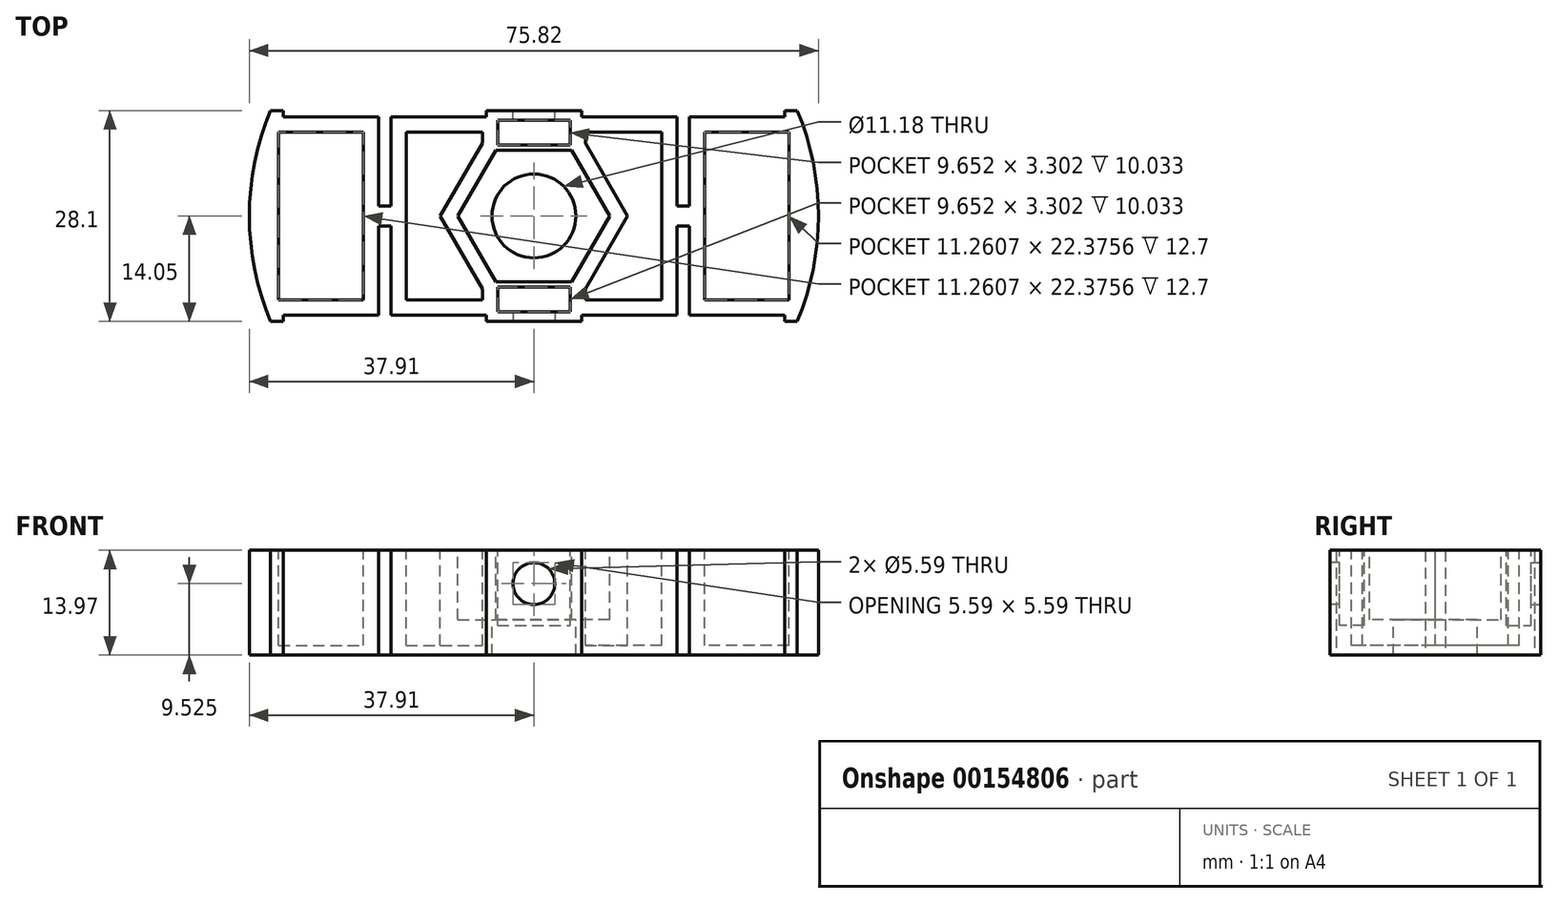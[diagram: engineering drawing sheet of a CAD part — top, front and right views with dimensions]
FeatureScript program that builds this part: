
annotation { "Feature Type Name" : "Feature", "Feature Type Description" : "" }
export const myFeature = defineFeature(function(context is Context, id is Id, definition is map)
    precondition{}
    {
        {
            var Q0;
            Q0=qCreatedBy(makeId("Top.planeOp"),FACE);
            var sketch = newSketch(context, id + "F0", { "sketchPlane" : qUnion([Q0])});
            skLineSegment(sketch, "E0", {"start": v(-37.9, 0) * mm, "end": v(0, 0) * mm, "construction": true});
            skLineSegment(sketch, "E1", {"start": v(-35.07, 14.05) * mm, "end": v(-33.4, 14.05) * mm});
            skArc(sketch, "E2.trimOffspring", {"start": v(-35.07, 14.05) * mm, "mid": v(-37.2, 7.16) * mm, "end": v(-37.9, 0) * mm});
            skLineSegment(sketch, "E3", {"start": v(-20.7, 13.22) * mm, "end": v(-20.7, 1.35) * mm});
            skLineSegment(sketch, "E4", {"start": v(-20.7, 1.35) * mm, "end": v(-19.05, 1.35) * mm});
            skLineSegment(sketch, "E5", {"start": v(-19.05, 1.35) * mm, "end": v(-19.05, 13.22) * mm});
            skLineSegment(sketch, "E6", {"start": v(-19.05, 13.22) * mm, "end": v(-6.35, 13.22) * mm});
            skLineSegment(sketch, "E7", {"start": v(-6.35, 13.22) * mm, "end": v(-6.35, 14.05) * mm});
            skLineSegment(sketch, "E8", {"start": v(-20.7, 13.22) * mm, "end": v(-33.4, 13.22) * mm});
            skLineSegment(sketch, "E9", {"start": v(-33.4, 13.22) * mm, "end": v(-33.4, 14.05) * mm});
            skLineSegment(sketch, "E10.trimOffspring", {"start": v(-6.35, 14.05) * mm, "end": v(0, 14.05) * mm});
            skLineSegment(sketch, "E11", {"start": v(0, 14.05) * mm, "end": v(0, 0) * mm, "construction": true});
            skLineSegment(sketch, "E12.MirrorCS", {"start": v(0, -14.05) * mm, "end": v(0, 0) * mm, "construction": true});
            skPoint(sketch, "E13.MirrorCS.end.orphan", {"position": v(-37.9, 0) * mm});
            skLineSegment(sketch, "E14", {"start": v(-37.9, 0) * mm, "end": v(0, 0) * mm});
            skLineSegment(sketch, "E15", {"start": v(0, 14.05) * mm, "end": v(0, 0) * mm});
            skSolve(sketch);
        }
        {
            var Q0;
            Q0 = qSketchRegion(id + "F0", true);
            extrude(context, id + "F1", {"entities" : qUnion([Q0]), "depth" : 9.52 * mm});
        }
        {
            var Q0;
            Q0=makeQuery(id+"F1.opExtrude","CAP_FACE",FACE,{"disambiguationData":[OSD([sQuery(id+"F0.wireOp",EDGE,"E1"),sQuery(id+"F0.wireOp",EDGE,"E2.trimOffspring"),sQuery(id+"F0.wireOp",EDGE,"E3"),sQuery(id+"F0.wireOp",EDGE,"E4"),sQuery(id+"F0.wireOp",EDGE,"E5"),sQuery(id+"F0.wireOp",EDGE,"E6"),sQuery(id+"F0.wireOp",EDGE,"E7"),sQuery(id+"F0.wireOp",EDGE,"E8"),sQuery(id+"F0.wireOp",EDGE,"E9"),sQuery(id+"F0.wireOp",EDGE,"E10.trimOffspring"),sQuery(id+"F0.wireOp",EDGE,"17128e08-2a4f-4ac8-b99a-ad05750c33720.MirrorCS"),sQuery(id+"F0.wireOp",EDGE,"17128e08-2a4f-4ac8-b99a-ad05750c33721.MirrorCS"),sQuery(id+"F0.wireOp",EDGE,"17128e08-2a4f-4ac8-b99a-ad05750c33722.MirrorCS"),sQuery(id+"F0.wireOp",EDGE,"17128e08-2a4f-4ac8-b99a-ad05750c33723.MirrorCS"),sQuery(id+"F0.wireOp",EDGE,"17128e08-2a4f-4ac8-b99a-ad05750c33724.MirrorCS"),sQuery(id+"F0.wireOp",EDGE,"17128e08-2a4f-4ac8-b99a-ad05750c33725.MirrorCS"),sQuery(id+"F0.wireOp",EDGE,"17128e08-2a4f-4ac8-b99a-ad05750c33726.MirrorCS"),sQuery(id+"F0.wireOp",EDGE,"17128e08-2a4f-4ac8-b99a-ad05750c33727.MirrorCS"),sQuery(id+"F0.wireOp",EDGE,"17128e08-2a4f-4ac8-b99a-ad05750c33728.MirrorCS"),sQuery(id+"F0.wireOp",EDGE,"17128e08-2a4f-4ac8-b99a-ad05750c33729.MirrorCS"),sQuery(id+"F0.wireOp",EDGE,"2adf77e0-dea9-4455-b5b0-009e9eeb048a0.MirrorCS"),sQuery(id+"F0.wireOp",EDGE,"2adf77e0-dea9-4455-b5b0-009e9eeb048a1.MirrorCS"),sQuery(id+"F0.wireOp",EDGE,"2adf77e0-dea9-4455-b5b0-009e9eeb048a2.MirrorCS"),sQuery(id+"F0.wireOp",EDGE,"2adf77e0-dea9-4455-b5b0-009e9eeb048a3.MirrorCS"),sQuery(id+"F0.wireOp",EDGE,"2adf77e0-dea9-4455-b5b0-009e9eeb048a4.MirrorCS"),sQuery(id+"F0.wireOp",EDGE,"2adf77e0-dea9-4455-b5b0-009e9eeb048a5.MirrorCS"),sQuery(id+"F0.wireOp",EDGE,"2adf77e0-dea9-4455-b5b0-009e9eeb048a6.MirrorCS"),sQuery(id+"F0.wireOp",EDGE,"2adf77e0-dea9-4455-b5b0-009e9eeb048a7.MirrorCS"),sQuery(id+"F0.wireOp",EDGE,"2adf77e0-dea9-4455-b5b0-009e9eeb048a8.MirrorCS"),sQuery(id+"F0.wireOp",EDGE,"2adf77e0-dea9-4455-b5b0-009e9eeb048a9.MirrorCS"),sQuery(id+"F0.wireOp",EDGE,"2adf77e0-dea9-4455-b5b0-009e9eeb048a10.MirrorCS"),sQuery(id+"F0.wireOp",EDGE,"2adf77e0-dea9-4455-b5b0-009e9eeb048a11.MirrorCS"),sQuery(id+"F0.wireOp",EDGE,"2adf77e0-dea9-4455-b5b0-009e9eeb048a12.MirrorCS"),sQuery(id+"F0.wireOp",EDGE,"2adf77e0-dea9-4455-b5b0-009e9eeb048a13.MirrorCS"),sQuery(id+"F0.wireOp",EDGE,"2adf77e0-dea9-4455-b5b0-009e9eeb048a15.MirrorCS"),sQuery(id+"F0.wireOp",EDGE,"2adf77e0-dea9-4455-b5b0-009e9eeb048a16.MirrorCS"),sQuery(id+"F0.wireOp",EDGE,"2adf77e0-dea9-4455-b5b0-009e9eeb048a18.MirrorCS"),sQuery(id+"F0.wireOp",EDGE,"2adf77e0-dea9-4455-b5b0-009e9eeb048a19.MirrorCS"),sQuery(id+"F0.wireOp",EDGE,"2adf77e0-dea9-4455-b5b0-009e9eeb048a20.MirrorCS"),sQuery(id+"F0.wireOp",EDGE,"E13.MirrorCS")])],"isStart":false});
            var sketch = newSketch(context, id + "F2", { "sketchPlane" : qUnion([Q0])});
            skCircle(sketch, "E16.cCircle", {"center": v(0, 0) * mm, "radius": 8.9 * mm, "construction": true});
            skLineSegment(sketch, "E16.0", {"start": v(10.27, 0) * mm, "end": v(5.13, -8.9) * mm});
            skLineSegment(sketch, "E16.1", {"start": v(5.13, -8.9) * mm, "end": v(-5.13, -8.89) * mm});
            skLineSegment(sketch, "E16.2", {"start": v(-5.13, -8.9) * mm, "end": v(-10.27, 0) * mm});
            skLineSegment(sketch, "E16.3", {"start": v(-10.27, 0) * mm, "end": v(-5.13, 8.9) * mm});
            skLineSegment(sketch, "E16.4", {"start": v(-5.13, 8.9) * mm, "end": v(5.13, 8.89) * mm});
            skLineSegment(sketch, "E16.5", {"start": v(5.13, 8.9) * mm, "end": v(10.27, 0) * mm});
            skPoint(sketch, "E16.0.midPoint", {"position": v(7.7, -4.45) * mm});
            skSolve(sketch);
        }
        {
            var Q0;
            Q0=makeQuery(id+"F2.imprint","IMPRINT",FACE,{"disambiguationData":[TD([[makeQuery(id+"F2.imprint","IMPRINT",EDGE,{"derivedFrom":sQuery(id+"F2.wireOp",EDGE,"E16.0")}),-1.0]])]});
            extrude(context, id + "F3", {"entities" : qUnion([Q0]), "operationType" : NewBodyOperationType.REMOVE, "oppositeDirection" : true, "depth" : 6.35 * mm});
        }
        {
            var Q0;
            Q0=makeQuery(id+"F1.opExtrude","CAP_FACE",FACE,{"disambiguationData":[OSD([sQuery(id+"F0.wireOp",EDGE,"E1"),sQuery(id+"F0.wireOp",EDGE,"E2.trimOffspring"),sQuery(id+"F0.wireOp",EDGE,"E3"),sQuery(id+"F0.wireOp",EDGE,"E4"),sQuery(id+"F0.wireOp",EDGE,"E5"),sQuery(id+"F0.wireOp",EDGE,"E6"),sQuery(id+"F0.wireOp",EDGE,"E7"),sQuery(id+"F0.wireOp",EDGE,"E8"),sQuery(id+"F0.wireOp",EDGE,"E9"),sQuery(id+"F0.wireOp",EDGE,"E10.trimOffspring"),sQuery(id+"F0.wireOp",EDGE,"17128e08-2a4f-4ac8-b99a-ad05750c33720.MirrorCS"),sQuery(id+"F0.wireOp",EDGE,"17128e08-2a4f-4ac8-b99a-ad05750c33721.MirrorCS"),sQuery(id+"F0.wireOp",EDGE,"17128e08-2a4f-4ac8-b99a-ad05750c33722.MirrorCS"),sQuery(id+"F0.wireOp",EDGE,"17128e08-2a4f-4ac8-b99a-ad05750c33723.MirrorCS"),sQuery(id+"F0.wireOp",EDGE,"17128e08-2a4f-4ac8-b99a-ad05750c33724.MirrorCS"),sQuery(id+"F0.wireOp",EDGE,"17128e08-2a4f-4ac8-b99a-ad05750c33725.MirrorCS"),sQuery(id+"F0.wireOp",EDGE,"17128e08-2a4f-4ac8-b99a-ad05750c33726.MirrorCS"),sQuery(id+"F0.wireOp",EDGE,"17128e08-2a4f-4ac8-b99a-ad05750c33727.MirrorCS"),sQuery(id+"F0.wireOp",EDGE,"17128e08-2a4f-4ac8-b99a-ad05750c33728.MirrorCS"),sQuery(id+"F0.wireOp",EDGE,"17128e08-2a4f-4ac8-b99a-ad05750c33729.MirrorCS"),sQuery(id+"F0.wireOp",EDGE,"2adf77e0-dea9-4455-b5b0-009e9eeb048a0.MirrorCS"),sQuery(id+"F0.wireOp",EDGE,"2adf77e0-dea9-4455-b5b0-009e9eeb048a1.MirrorCS"),sQuery(id+"F0.wireOp",EDGE,"2adf77e0-dea9-4455-b5b0-009e9eeb048a2.MirrorCS"),sQuery(id+"F0.wireOp",EDGE,"2adf77e0-dea9-4455-b5b0-009e9eeb048a3.MirrorCS"),sQuery(id+"F0.wireOp",EDGE,"2adf77e0-dea9-4455-b5b0-009e9eeb048a4.MirrorCS"),sQuery(id+"F0.wireOp",EDGE,"2adf77e0-dea9-4455-b5b0-009e9eeb048a5.MirrorCS"),sQuery(id+"F0.wireOp",EDGE,"2adf77e0-dea9-4455-b5b0-009e9eeb048a6.MirrorCS"),sQuery(id+"F0.wireOp",EDGE,"2adf77e0-dea9-4455-b5b0-009e9eeb048a7.MirrorCS"),sQuery(id+"F0.wireOp",EDGE,"2adf77e0-dea9-4455-b5b0-009e9eeb048a8.MirrorCS"),sQuery(id+"F0.wireOp",EDGE,"2adf77e0-dea9-4455-b5b0-009e9eeb048a9.MirrorCS"),sQuery(id+"F0.wireOp",EDGE,"2adf77e0-dea9-4455-b5b0-009e9eeb048a10.MirrorCS"),sQuery(id+"F0.wireOp",EDGE,"2adf77e0-dea9-4455-b5b0-009e9eeb048a11.MirrorCS"),sQuery(id+"F0.wireOp",EDGE,"2adf77e0-dea9-4455-b5b0-009e9eeb048a12.MirrorCS"),sQuery(id+"F0.wireOp",EDGE,"2adf77e0-dea9-4455-b5b0-009e9eeb048a13.MirrorCS"),sQuery(id+"F0.wireOp",EDGE,"2adf77e0-dea9-4455-b5b0-009e9eeb048a15.MirrorCS"),sQuery(id+"F0.wireOp",EDGE,"2adf77e0-dea9-4455-b5b0-009e9eeb048a16.MirrorCS"),sQuery(id+"F0.wireOp",EDGE,"2adf77e0-dea9-4455-b5b0-009e9eeb048a18.MirrorCS"),sQuery(id+"F0.wireOp",EDGE,"2adf77e0-dea9-4455-b5b0-009e9eeb048a19.MirrorCS"),sQuery(id+"F0.wireOp",EDGE,"2adf77e0-dea9-4455-b5b0-009e9eeb048a20.MirrorCS"),sQuery(id+"F0.wireOp",EDGE,"E13.MirrorCS")])],"isStart":false});
            var sketch = newSketch(context, id + "F4", { "sketchPlane" : qUnion([Q0])});
            skLineSegment(sketch, "E17.bottom", {"start": v(-4.83, -9.47) * mm, "end": v(4.83, -9.47) * mm});
            skLineSegment(sketch, "E17.top", {"start": v(-4.83, -12.78) * mm, "end": v(4.83, -12.78) * mm});
            skLineSegment(sketch, "E17.left", {"start": v(-4.83, -9.47) * mm, "end": v(-4.83, -12.78) * mm});
            skLineSegment(sketch, "E17.right", {"start": v(4.83, -9.47) * mm, "end": v(4.83, -12.78) * mm});
            skLineSegment(sketch, "E18", {"start": v(-12.78, 0) * mm, "end": v(12.46, 0) * mm, "construction": true});
            skLineSegment(sketch, "E19.MirrorCS", {"start": v(-4.83, 9.47) * mm, "end": v(4.83, 9.47) * mm});
            skLineSegment(sketch, "E20.MirrorCS", {"start": v(-4.83, 12.78) * mm, "end": v(4.83, 12.78) * mm});
            skLineSegment(sketch, "E21.MirrorCS", {"start": v(-4.83, 9.47) * mm, "end": v(-4.83, 12.78) * mm});
            skLineSegment(sketch, "E22.MirrorCS", {"start": v(4.83, 9.47) * mm, "end": v(4.83, 12.78) * mm});
            skSolve(sketch);
        }
        {
            var Q0;
            Q0 = qSketchRegion(id + "F4", true);
            extrude(context, id + "F5", {"entities" : qUnion([Q0]), "operationType" : NewBodyOperationType.REMOVE, "oppositeDirection" : true, "depth" : 5.6 * mm});
        }
        {
            var Q0;
            Q0=makeQuery(id+"F1.opExtrude","CAP_FACE",FACE,{"disambiguationData":[OSD([sQuery(id+"F0.wireOp",EDGE,"E1"),sQuery(id+"F0.wireOp",EDGE,"E2.trimOffspring"),sQuery(id+"F0.wireOp",EDGE,"E3"),sQuery(id+"F0.wireOp",EDGE,"E4"),sQuery(id+"F0.wireOp",EDGE,"E5"),sQuery(id+"F0.wireOp",EDGE,"E6"),sQuery(id+"F0.wireOp",EDGE,"E7"),sQuery(id+"F0.wireOp",EDGE,"E8"),sQuery(id+"F0.wireOp",EDGE,"E9"),sQuery(id+"F0.wireOp",EDGE,"E10.trimOffspring"),sQuery(id+"F0.wireOp",EDGE,"E14"),sQuery(id+"F0.wireOp",EDGE,"E15")])],"isStart":false});
            var sketch = newSketch(context, id + "F6", { "sketchPlane" : qUnion([Q0])});
            skCircle(sketch, "E23.cCircle", {"center": v(0, 0) * mm, "radius": 8.76 * mm, "construction": true});
            skLineSegment(sketch, "E23.0", {"start": v(5.06, -8.76) * mm, "end": v(-5.06, -8.76) * mm});
            skLineSegment(sketch, "E23.1", {"start": v(-5.06, -8.76) * mm, "end": v(-10.12, 0) * mm});
            skLineSegment(sketch, "E23.2", {"start": v(-10.12, 0) * mm, "end": v(-5.06, 8.76) * mm});
            skLineSegment(sketch, "E23.3", {"start": v(-5.06, 8.76) * mm, "end": v(5.06, 8.76) * mm});
            skLineSegment(sketch, "E23.4", {"start": v(5.06, 8.76) * mm, "end": v(10.12, 0) * mm});
            skLineSegment(sketch, "E23.5", {"start": v(10.12, 0) * mm, "end": v(5.06, -8.76) * mm});
            skPoint(sketch, "E23.0.midPoint", {"position": v(0, -8.76) * mm});
            skSolve(sketch);
        }
        {
            var Q0;
            Q0 = qSketchRegion(id + "F6", true);
            extrude(context, id + "F7", {"entities" : qUnion([Q0]), "operationType" : NewBodyOperationType.REMOVE, "oppositeDirection" : true, "depth" : 4.83 * mm});
        }
        {
            var Q0;
            Q0=makeQuery(id+"F7.boolean.opBoolean","COPY",FACE,{"derivedFrom":makeQuery(id+"F7.opExtrude","CAP_FACE",FACE,{"disambiguationData":[OSD([sQuery(id+"F6.wireOp",EDGE,"E23.0"),sQuery(id+"F6.wireOp",EDGE,"E23.1"),sQuery(id+"F6.wireOp",EDGE,"E23.2"),sQuery(id+"F6.wireOp",EDGE,"E23.3"),sQuery(id+"F6.wireOp",EDGE,"E23.4"),sQuery(id+"F6.wireOp",EDGE,"E23.5")])],"isStart":false})});
            var sketch = newSketch(context, id + "F8", { "sketchPlane" : qUnion([Q0])});
            skCircle(sketch, "E24", {"center": v(0, 0) * mm, "radius": 5.59 * mm});
            skSolve(sketch);
        }
        {
            var Q0;
            {var subQ0=sQuery(id+"F8.wireOp",EDGE,"E24");var subQ1=makeQuery(id+"F7.opExtrude","CAP_FACE",FACE,{"disambiguationData":[OSD([sQuery(id+"F6.wireOp",EDGE,"E23.0"),sQuery(id+"F6.wireOp",EDGE,"E23.1"),sQuery(id+"F6.wireOp",EDGE,"E23.2"),sQuery(id+"F6.wireOp",EDGE,"E23.3"),sQuery(id+"F6.wireOp",EDGE,"E23.4"),sQuery(id+"F6.wireOp",EDGE,"E23.5")])],"isStart":false});var subQ2=makeQuery(id+"F7.boolean.opBoolean","INTERSECT",EDGE,{"derivedFrom":[makeQuery(id+"F1.opExtrude","SWEPT_FACE",FACE,{"disambiguationData":[OSD([sQuery(id+"F0.wireOp",EDGE,"E14")])]}),subQ1]});var subQ3=makeQuery(id+"F8.imprint","INTERSECT",VERTEX,{"derivedFrom":[subQ2,subQ0]});Q0=makeQuery(id+"F8.imprint","IMPRINT",FACE,{"disambiguationData":[TD([[makeQuery(id+"F8.imprint","IMPRINT",EDGE,{"disambiguationData":[TD([[subQ3,1.0]])],"derivedFrom":subQ0}),1.0]])]});}
            extrude(context, id + "F9", {"entities" : qUnion([Q0]), "operationType" : NewBodyOperationType.REMOVE, "endBound" : BoundingType.UP_TO_NEXT, "oppositeDirection" : true, "depth" : 25.4 * mm});
        }
        {
            var Q0;
            Q0=makeQuery(id+"F1.opExtrude","SWEPT_FACE",FACE,{"disambiguationData":[OSD([sQuery(id+"F0.wireOp",EDGE,"E10.trimOffspring")])]});
            var sketch = newSketch(context, id + "F10", { "sketchPlane" : qUnion([Q0])});
            skCircle(sketch, "E25", {"center": v(0, 9.53) * mm, "radius": 2.8 * mm});
            skSolve(sketch);
        }
        {
            var Q0;
            {var subQ0=sQuery(id+"F10.wireOp",EDGE,"E25");var subQ1=sQuery(id+"F0.wireOp",EDGE,"E10.trimOffspring");var subQ4=makeQuery(id+"F1.opExtrude","CAP_EDGE",EDGE,{"disambiguationData":[OSD([subQ1])],"isStart":false});var subQ5=makeQuery(id+"F10.imprint","INTERSECT",VERTEX,{"derivedFrom":[subQ4,subQ0]});Q0=makeQuery(id+"F10.imprint","IMPRINT",FACE,{"disambiguationData":[TD([[makeQuery(id+"F10.imprint","IMPRINT",EDGE,{"disambiguationData":[TD([[subQ5,-1.0]])],"derivedFrom":subQ0}),1.0]])]});}
            var Q1;
            {var subQ0=sQuery(id+"F10.wireOp",EDGE,"E25");var subQ1=sQuery(id+"F0.wireOp",EDGE,"E10.trimOffspring");var subQ4=makeQuery(id+"F1.opExtrude","CAP_EDGE",EDGE,{"disambiguationData":[OSD([subQ1])],"isStart":false});var subQ5=makeQuery(id+"F10.imprint","INTERSECT",VERTEX,{"derivedFrom":[subQ4,subQ0]});Q1=makeQuery(id+"F10.imprint","IMPRINT",FACE,{"disambiguationData":[TD([[makeQuery(id+"F10.imprint","IMPRINT",EDGE,{"disambiguationData":[TD([[subQ5,1.0]])],"derivedFrom":subQ0}),1.0]])]});}
            extrude(context, id + "F11", {"entities" : qUnion([Q0, Q1]), "operationType" : NewBodyOperationType.REMOVE, "oppositeDirection" : true, "depth" : 1.78 * mm});
        }
        {
            var Q0;
            Q0=makeQuery(id+"F1.opExtrude","SWEPT_BODY",BODY,{"disambiguationData":[OSD([sQuery(id+"F0.wireOp",EDGE,"E1"),sQuery(id+"F0.wireOp",EDGE,"E2.trimOffspring"),sQuery(id+"F0.wireOp",EDGE,"E3"),sQuery(id+"F0.wireOp",EDGE,"E4"),sQuery(id+"F0.wireOp",EDGE,"E5"),sQuery(id+"F0.wireOp",EDGE,"E6"),sQuery(id+"F0.wireOp",EDGE,"E7"),sQuery(id+"F0.wireOp",EDGE,"E8"),sQuery(id+"F0.wireOp",EDGE,"E9"),sQuery(id+"F0.wireOp",EDGE,"E10.trimOffspring"),sQuery(id+"F0.wireOp",EDGE,"E14"),sQuery(id+"F0.wireOp",EDGE,"E15")])]});
            var Q1;
            Q1=qCreatedBy(makeId("Front.planeOp"),FACE);
            mirror(context, id + "F12", {"operationType" : NewBodyOperationType.ADD, "entities" : qUnion([Q0]), "mirrorPlane" : qUnion([Q1])});
        }
        {
            var Q0;
            Q0=makeQuery(id+"F1.opExtrude","SWEPT_BODY",BODY,{"disambiguationData":[OSD([sQuery(id+"F0.wireOp",EDGE,"E1"),sQuery(id+"F0.wireOp",EDGE,"E2.trimOffspring"),sQuery(id+"F0.wireOp",EDGE,"E3"),sQuery(id+"F0.wireOp",EDGE,"E4"),sQuery(id+"F0.wireOp",EDGE,"E5"),sQuery(id+"F0.wireOp",EDGE,"E6"),sQuery(id+"F0.wireOp",EDGE,"E7"),sQuery(id+"F0.wireOp",EDGE,"E8"),sQuery(id+"F0.wireOp",EDGE,"E9"),sQuery(id+"F0.wireOp",EDGE,"E10.trimOffspring"),sQuery(id+"F0.wireOp",EDGE,"E14"),sQuery(id+"F0.wireOp",EDGE,"E15")])]});
            var Q1;
            Q1=qCreatedBy(makeId("Right.planeOp"),FACE);
            mirror(context, id + "F13", {"operationType" : NewBodyOperationType.ADD, "entities" : qUnion([Q0]), "mirrorPlane" : qUnion([Q1])});
        }
        {
            var Q0;
            {var subQ0=makeQuery(id+"F1.opExtrude","CAP_FACE",FACE,{"disambiguationData":[OSD([sQuery(id+"F0.wireOp",EDGE,"E1"),sQuery(id+"F0.wireOp",EDGE,"E2.trimOffspring"),sQuery(id+"F0.wireOp",EDGE,"E3"),sQuery(id+"F0.wireOp",EDGE,"E4"),sQuery(id+"F0.wireOp",EDGE,"E5"),sQuery(id+"F0.wireOp",EDGE,"E6"),sQuery(id+"F0.wireOp",EDGE,"E7"),sQuery(id+"F0.wireOp",EDGE,"E8"),sQuery(id+"F0.wireOp",EDGE,"E9"),sQuery(id+"F0.wireOp",EDGE,"E10.trimOffspring"),sQuery(id+"F0.wireOp",EDGE,"E14"),sQuery(id+"F0.wireOp",EDGE,"E15")])],"isStart":false});var subQ1=makeQuery(id+"F12.boolean.opBoolean","MERGE",FACE,{"derivedFrom":[subQ0,makeQuery(id+"F12.opPattern","COPY",FACE,{"derivedFrom":subQ0,"instanceName":"1"})]});Q0=makeQuery(id+"F13.boolean.opBoolean","MERGE",FACE,{"derivedFrom":[subQ1,makeQuery(id+"F13.opPattern","COPY",FACE,{"derivedFrom":subQ1,"instanceName":"1"})]});}
            var Q1;
            Q1=makeQuery(id+"F13.opPattern","COPY",VERTEX,{"derivedFrom":makeQuery(id+"F1.opExtrude","CAP_VERTEX",VERTEX,{"disambiguationData":[OSD([sQuery(id+"F0.wireOp",EDGE,"E1"),sQuery(id+"F0.wireOp",EDGE,"E2.trimOffspring")])],"isStart":false}),"instanceName":"1"});
            cPlane(context, id + "F14", {"entities" : qUnion([Q0, Q1]), "cplaneType" : CPlaneType.PLANE_POINT, "offset" : 25.4 * mm, "width" : 152.4 * mm, "height" : 152.4 * mm});
        }
        {
            var Q0;
            Q0=makeQuery(id+"F1.opExtrude","SWEPT_BODY",BODY,{"disambiguationData":[OSD([sQuery(id+"F0.wireOp",EDGE,"E1"),sQuery(id+"F0.wireOp",EDGE,"E2.trimOffspring"),sQuery(id+"F0.wireOp",EDGE,"E3"),sQuery(id+"F0.wireOp",EDGE,"E4"),sQuery(id+"F0.wireOp",EDGE,"E5"),sQuery(id+"F0.wireOp",EDGE,"E6"),sQuery(id+"F0.wireOp",EDGE,"E7"),sQuery(id+"F0.wireOp",EDGE,"E8"),sQuery(id+"F0.wireOp",EDGE,"E9"),sQuery(id+"F0.wireOp",EDGE,"E10.trimOffspring"),sQuery(id+"F0.wireOp",EDGE,"E14"),sQuery(id+"F0.wireOp",EDGE,"E15")])]});
            var Q1;
            Q1=qCreatedBy(id+"F14.planeOp",FACE);
            mirror(context, id + "F15", {"operationType" : NewBodyOperationType.ADD, "entities" : qUnion([Q0]), "mirrorPlane" : qUnion([Q1])});
        }
        {
            var Q0;
            {var subQ0=makeQuery(id+"F1.opExtrude","CAP_FACE",FACE,{"disambiguationData":[OSD([sQuery(id+"F0.wireOp",EDGE,"E1"),sQuery(id+"F0.wireOp",EDGE,"E2.trimOffspring"),sQuery(id+"F0.wireOp",EDGE,"E3"),sQuery(id+"F0.wireOp",EDGE,"E4"),sQuery(id+"F0.wireOp",EDGE,"E5"),sQuery(id+"F0.wireOp",EDGE,"E6"),sQuery(id+"F0.wireOp",EDGE,"E7"),sQuery(id+"F0.wireOp",EDGE,"E8"),sQuery(id+"F0.wireOp",EDGE,"E9"),sQuery(id+"F0.wireOp",EDGE,"E10.trimOffspring"),sQuery(id+"F0.wireOp",EDGE,"E14"),sQuery(id+"F0.wireOp",EDGE,"E15")])],"isStart":true});var subQ1=makeQuery(id+"F12.boolean.opBoolean","MERGE",FACE,{"derivedFrom":[subQ0,makeQuery(id+"F12.opPattern","COPY",FACE,{"derivedFrom":subQ0,"instanceName":"1"})]});Q0=makeQuery(id+"F15.opPattern","COPY",FACE,{"derivedFrom":makeQuery(id+"F13.boolean.opBoolean","MERGE",FACE,{"derivedFrom":[subQ1,makeQuery(id+"F13.opPattern","COPY",FACE,{"derivedFrom":subQ1,"instanceName":"1"})]}),"instanceName":"1"});}
            var sketch = newSketch(context, id + "F16", { "sketchPlane" : qUnion([Q0])});
            skLineSegment(sketch, "E26.bottom", {"start": v(40.4, -16.4) * mm, "end": v(-40.4, -16.4) * mm});
            skLineSegment(sketch, "E26.top", {"start": v(40.4, 16.4) * mm, "end": v(-40.4, 16.4) * mm});
            skLineSegment(sketch, "E26.left", {"start": v(40.4, -16.4) * mm, "end": v(40.4, 16.4) * mm});
            skLineSegment(sketch, "E26.right", {"start": v(-40.4, -16.4) * mm, "end": v(-40.4, 16.4) * mm});
            skPoint(sketch, "E26.middle", {"position": v(0, 0) * mm});
            skSolve(sketch);
        }
        {
            var Q0;
            Q0 = qSketchRegion(id + "F16", true);
            extrude(context, id + "F17", {"entities" : qUnion([Q0]), "operationType" : NewBodyOperationType.REMOVE, "oppositeDirection" : true, "depth" : 5.08 * mm});
        }
        {
            var Q0;
            Q0=makeQuery(id+"F17.boolean.opBoolean","COPY",FACE,{"derivedFrom":makeQuery(id+"F17.opExtrude","CAP_FACE",FACE,{"disambiguationData":[OSD([sQuery(id+"F16.wireOp",EDGE,"E26.bottom"),sQuery(id+"F16.wireOp",EDGE,"E26.top"),sQuery(id+"F16.wireOp",EDGE,"E26.left"),sQuery(id+"F16.wireOp",EDGE,"E26.right")])],"isStart":false})});
            var sketch = newSketch(context, id + "F18", { "sketchPlane" : qUnion([Q0])});
            skLineSegment(sketch, "E27.bottom", {"start": v(-34, 11.19) * mm, "end": v(-22.73, 11.19) * mm});
            skLineSegment(sketch, "E27.top", {"start": v(-34, -11.19) * mm, "end": v(-22.73, -11.19) * mm});
            skLineSegment(sketch, "E27.left", {"start": v(-34, 11.19) * mm, "end": v(-34, -11.19) * mm});
            skLineSegment(sketch, "E27.right", {"start": v(-22.73, 11.19) * mm, "end": v(-22.73, -11.19) * mm});
            skPoint(sketch, "E28.firstSnap0", {"position": v(-28.36, 11.19) * mm});
            skLineSegment(sketch, "E28.bottom", {"start": v(-17.02, 11.19) * mm, "end": v(-6.86, 11.19) * mm});
            skLineSegment(sketch, "E28.top", {"start": v(-17.02, -11.19) * mm, "end": v(-6.86, -11.19) * mm});
            skLineSegment(sketch, "E28.left", {"start": v(-17.02, 11.19) * mm, "end": v(-17.02, -11.19) * mm});
            skLineSegment(sketch, "E28.right", {"start": v(-6.86, 11.19) * mm, "end": v(-6.86, 9.71) * mm});
            skLineSegment(sketch, "E29", {"start": v(-6.86, 9.71) * mm, "end": v(-12.46, 0) * mm});
            skLineSegment(sketch, "E30", {"start": v(-12.46, 0) * mm, "end": v(-6.86, -9.71) * mm});
            skLineSegment(sketch, "E31.trimOffspring", {"start": v(-6.86, -9.71) * mm, "end": v(-6.86, -11.19) * mm});
            skLineSegment(sketch, "E32", {"start": v(0, 14.05) * mm, "end": v(0, -14.05) * mm, "construction": true});
            skLineSegment(sketch, "E33.MirrorCS", {"start": v(6.86, 11.19) * mm, "end": v(6.86, 9.71) * mm});
            skLineSegment(sketch, "E34.MirrorCS", {"start": v(6.86, -9.71) * mm, "end": v(6.86, -11.19) * mm});
            skLineSegment(sketch, "E35.MirrorCS", {"start": v(6.86, 9.71) * mm, "end": v(12.46, 0) * mm});
            skLineSegment(sketch, "E36.MirrorCS", {"start": v(34, 11.19) * mm, "end": v(22.73, 11.19) * mm});
            skLineSegment(sketch, "E37.MirrorCS", {"start": v(17.02, 11.19) * mm, "end": v(6.86, 11.19) * mm});
            skLineSegment(sketch, "E38.MirrorCS", {"start": v(17.02, -11.19) * mm, "end": v(6.86, -11.19) * mm});
            skLineSegment(sketch, "E39.MirrorCS", {"start": v(17.02, 11.19) * mm, "end": v(17.02, -11.19) * mm});
            skLineSegment(sketch, "E40.MirrorCS", {"start": v(34, -11.19) * mm, "end": v(22.73, -11.19) * mm});
            skLineSegment(sketch, "E41.MirrorCS", {"start": v(34, 11.19) * mm, "end": v(34, -11.19) * mm});
            skLineSegment(sketch, "E42.MirrorCS", {"start": v(12.46, 0) * mm, "end": v(6.86, -9.71) * mm});
            skPoint(sketch, "E43.MirrorP", {"position": v(28.36, 11.19) * mm});
            skLineSegment(sketch, "E44.MirrorCS", {"start": v(22.73, 11.19) * mm, "end": v(22.73, -11.19) * mm});
            skSolve(sketch);
        }
        {
            var Q0;
            Q0 = qSketchRegion(id + "F18", true);
            extrude(context, id + "F19", {"entities" : qUnion([Q0]), "operationType" : NewBodyOperationType.REMOVE, "oppositeDirection" : true, "depth" : 12.7 * mm});
        }
        {
            var Q0;
            Q0=makeQuery(id+"F1.opExtrude","SWEPT_BODY",BODY,{"disambiguationData":[OSD([sQuery(id+"F0.wireOp",EDGE,"E1"),sQuery(id+"F0.wireOp",EDGE,"E2.trimOffspring"),sQuery(id+"F0.wireOp",EDGE,"E3"),sQuery(id+"F0.wireOp",EDGE,"E4"),sQuery(id+"F0.wireOp",EDGE,"E5"),sQuery(id+"F0.wireOp",EDGE,"E6"),sQuery(id+"F0.wireOp",EDGE,"E7"),sQuery(id+"F0.wireOp",EDGE,"E8"),sQuery(id+"F0.wireOp",EDGE,"E9"),sQuery(id+"F0.wireOp",EDGE,"E10.trimOffspring"),sQuery(id+"F0.wireOp",EDGE,"E14"),sQuery(id+"F0.wireOp",EDGE,"E15")])]});
            var Q1;
            Q1=qCreatedBy(makeId("Front.planeOp"),FACE);
            mirror(context, id + "F20", {"operationType" : NewBodyOperationType.ADD, "entities" : qUnion([Q0]), "mirrorPlane" : qUnion([Q1])});
        }
    });
